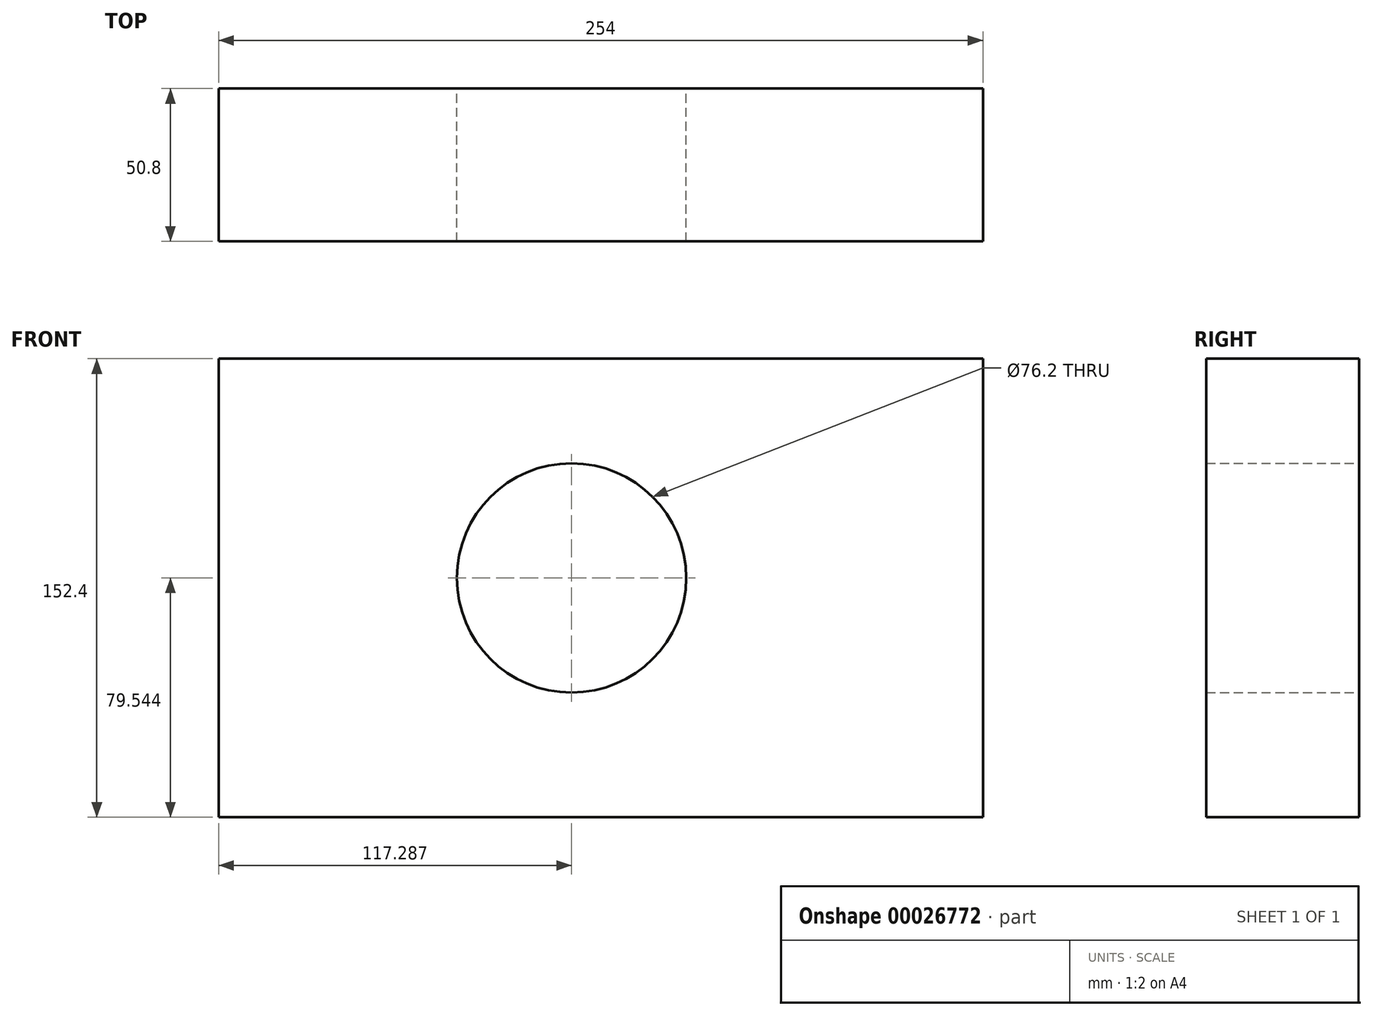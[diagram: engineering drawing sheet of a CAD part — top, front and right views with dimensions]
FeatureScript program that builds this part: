
annotation { "Feature Type Name" : "Feature", "Feature Type Description" : "" }
export const myFeature = defineFeature(function(context is Context, id is Id, definition is map)
    precondition{}
    {
        {
            var Q0;
            Q0=qCreatedBy(makeId("Front.planeOp"),FACE);
            var sketch = newSketch(context, id + "F0", { "sketchPlane" : qUnion([Q0])});
            skLineSegment(sketch, "E0.bottom", {"start": v(-123.5, -55.6) * mm, "end": v(130.5, -55.6) * mm});
            skLineSegment(sketch, "E0.top", {"start": v(-123.5, 96.8) * mm, "end": v(130.5, 96.8) * mm});
            skLineSegment(sketch, "E0.left", {"start": v(-123.5, -55.6) * mm, "end": v(-123.5, 96.8) * mm});
            skLineSegment(sketch, "E0.right", {"start": v(130.5, -55.6) * mm, "end": v(130.5, 96.8) * mm});
            skCircle(sketch, "E1", {"center": v(-6.21, 23.93) * mm, "radius": 38.1 * mm});
            skSolve(sketch);
        }
        {
            var Q0;
            Q0=makeQuery(id+"F0.imprint","IMPRINT",FACE,{"disambiguationData":[TD([[makeQuery(id+"F0.imprint","IMPRINT",EDGE,{"derivedFrom":sQuery(id+"F0.wireOp",EDGE,"E0.bottom")}),1.0]])]});
            extrude(context, id + "F1", {"entities" : qUnion([Q0]), "depth" : 50.8 * mm});
        }
    });
